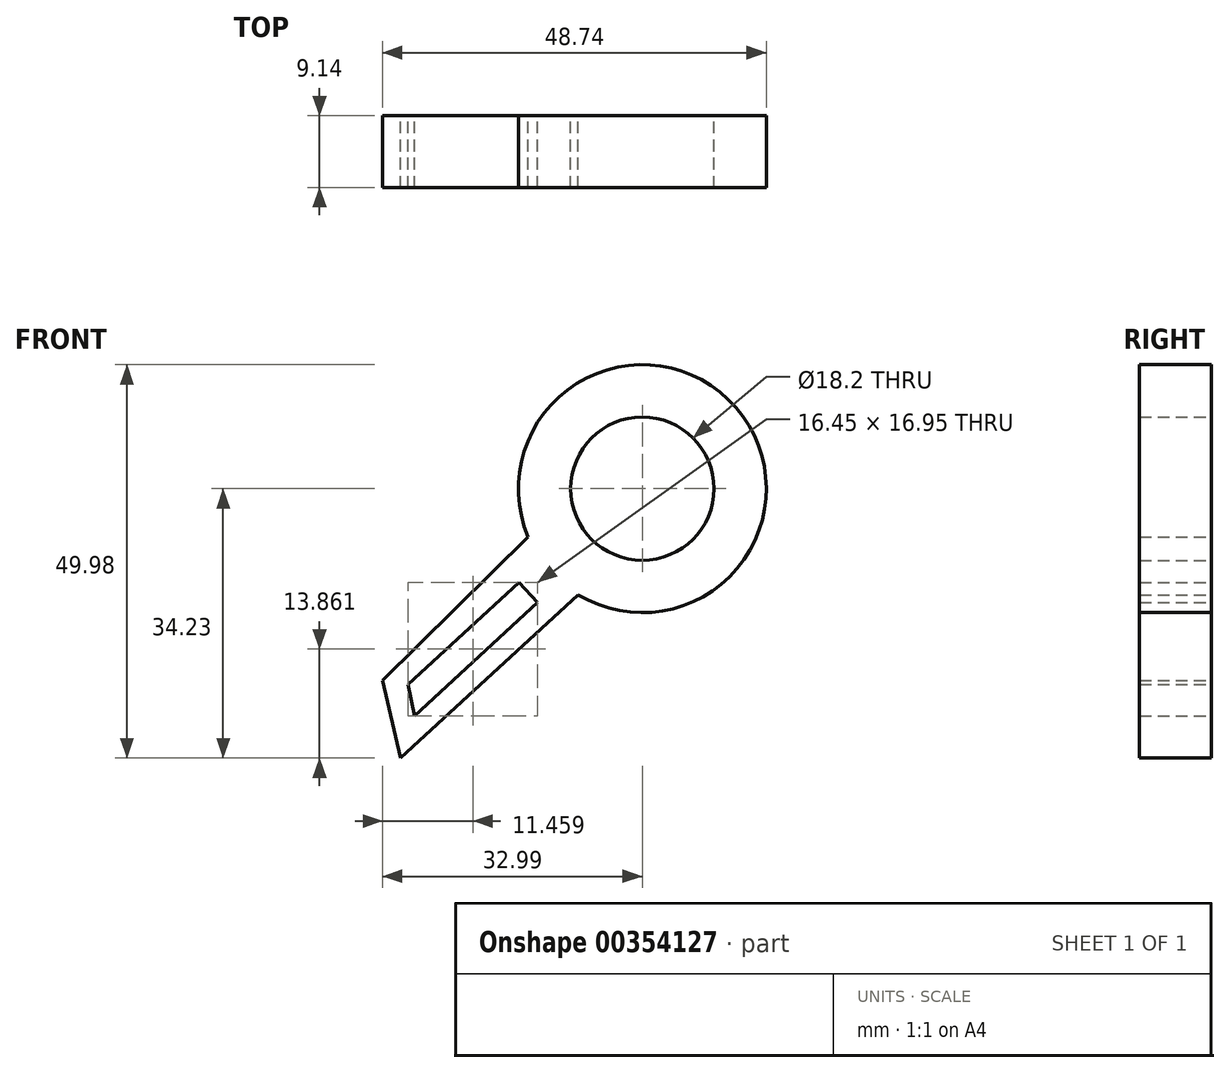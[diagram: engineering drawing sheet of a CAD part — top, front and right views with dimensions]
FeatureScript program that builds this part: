
annotation { "Feature Type Name" : "Feature", "Feature Type Description" : "" }
export const myFeature = defineFeature(function(context is Context, id is Id, definition is map)
    precondition{}
    {
        {
            var Q0;
            Q0=qCreatedBy(makeId("Front.planeOp"),FACE);
            var sketch = newSketch(context, id + "F0", { "sketchPlane" : qUnion([Q0])});
            skLineSegment(sketch, "E0", {"start": v(1.03, 12.96) * mm, "end": v(21.48, 32.44) * mm});
            skLineSegment(sketch, "E1", {"start": v(3.64, 4.81) * mm, "end": v(28.39, 26.1) * mm});
            skCircle(sketch, "E2", {"center": v(33, 37.33) * mm, "radius": 15.75 * mm});
            skCircle(sketch, "E3.MirrorC", {"center": v(33, 37.33) * mm, "radius": 9.1 * mm});
            skSolve(sketch);
        }
        {
            var Q0;
            Q0=makeQuery(id+"F0.imprint","IMPRINT",FACE,{"disambiguationData":[TD([[makeQuery(id+"F0.imprint","IMPRINT",EDGE,{"derivedFrom":sQuery(id+"F0.wireOp",EDGE,"E2")}),1.0]])]});
            extrude(context, id + "F1", {"entities" : qUnion([Q0]), "depth" : 9.14 * mm});
        }
        {
            var Q0;
            Q0=qCreatedBy(makeId("Front.planeOp"),FACE);
            var sketch = newSketch(context, id + "F2", { "sketchPlane" : qUnion([Q0])});
            skLineSegment(sketch, "E4", {"start": v(20.15, 32.8) * mm, "end": v(26.77, 25.61) * mm});
            skLineSegment(sketch, "E5", {"start": v(26.77, 25.61) * mm, "end": v(2.3, 3.1) * mm});
            skLineSegment(sketch, "E6", {"start": v(2.3, 3.1) * mm, "end": v(0, 12.95) * mm});
            skLineSegment(sketch, "E7", {"start": v(0, 12.95) * mm, "end": v(20.15, 32.8) * mm});
            skLineSegment(sketch, "E8", {"start": v(3.23, 12.48) * mm, "end": v(17.32, 25.44) * mm});
            skLineSegment(sketch, "E9", {"start": v(17.32, 25.44) * mm, "end": v(19.68, 22.86) * mm});
            skLineSegment(sketch, "E10", {"start": v(19.68, 22.86) * mm, "end": v(4.06, 8.48) * mm});
            skLineSegment(sketch, "E11", {"start": v(4.06, 8.48) * mm, "end": v(3.23, 12.48) * mm});
            skSolve(sketch);
        }
        {
            var Q0;
            Q0=qSketchRegion(id+"F2",true);
            extrude(context, id + "F3", {"entities" : qUnion([Q0]), "operationType" : NewBodyOperationType.ADD, "depth" : 9.14 * mm});
        }
    });
